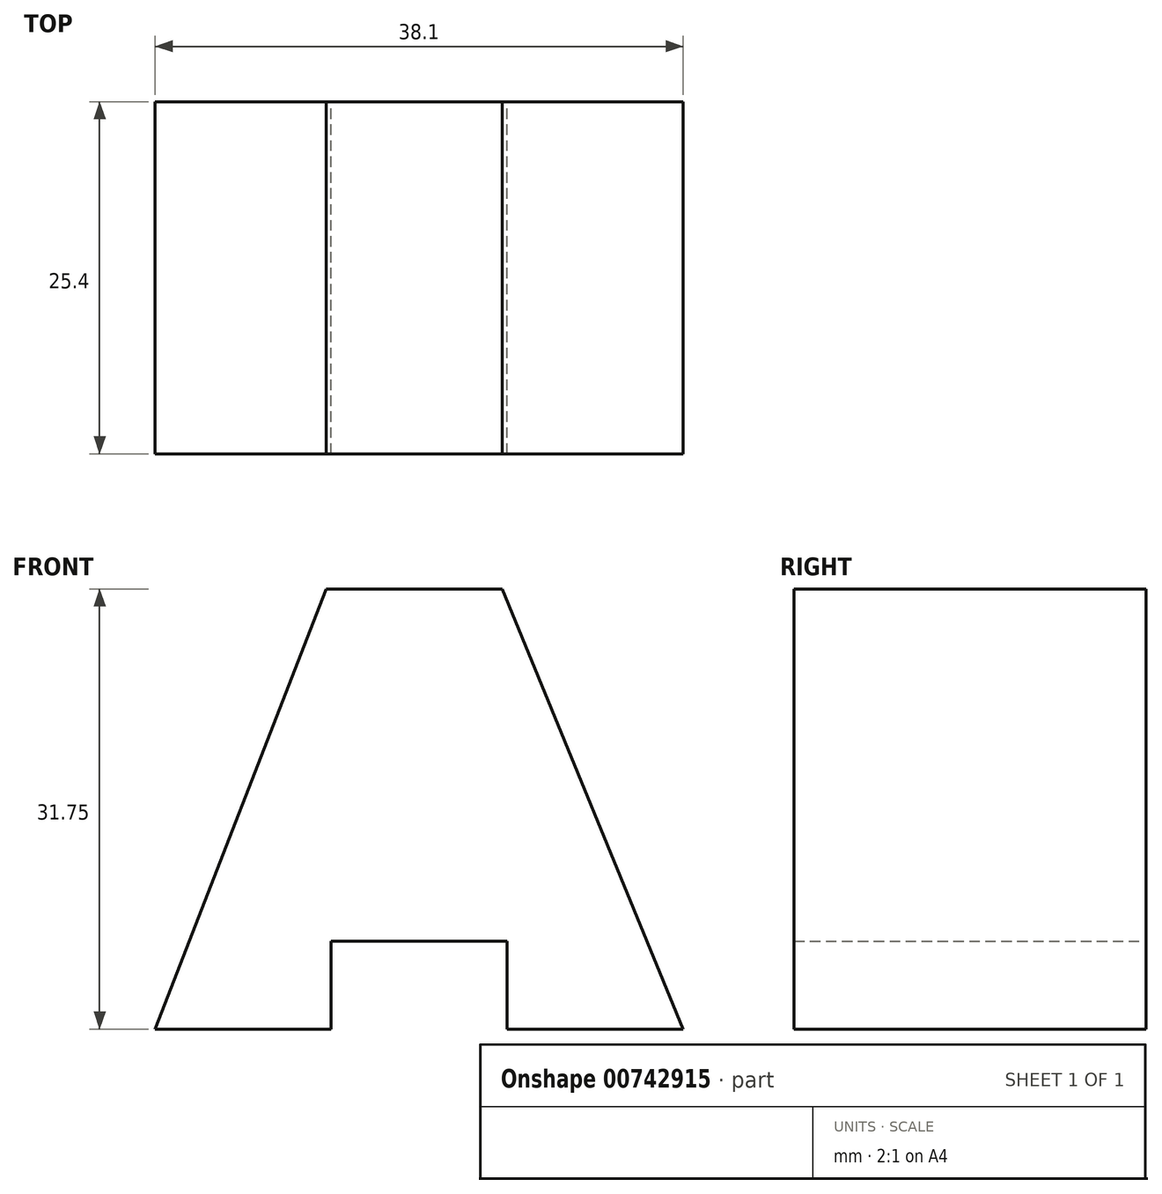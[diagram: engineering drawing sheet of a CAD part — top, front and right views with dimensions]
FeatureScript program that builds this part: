
annotation { "Feature Type Name" : "Feature", "Feature Type Description" : "" }
export const myFeature = defineFeature(function(context is Context, id is Id, definition is map)
    precondition{}
    {
        {
            var Q0;
            Q0=qCreatedBy(makeId("Front.planeOp"),FACE);
            var sketch = newSketch(context, id + "F0", { "sketchPlane" : qUnion([Q0])});
            skLineSegment(sketch, "E0", {"start": v(0, 0) * mm, "end": v(12.7, 0) * mm});
            skLineSegment(sketch, "E1", {"start": v(12.7, 0) * mm, "end": v(12.7, 6.35) * mm});
            skLineSegment(sketch, "E2", {"start": v(12.7, 6.35) * mm, "end": v(25.4, 6.35) * mm});
            skLineSegment(sketch, "E3", {"start": v(25.4, 6.35) * mm, "end": v(25.4, 0) * mm});
            skLineSegment(sketch, "E4", {"start": v(25.4, 0) * mm, "end": v(38.1, 0) * mm});
            skLineSegment(sketch, "E5", {"start": v(38.1, 0) * mm, "end": v(25.03, 31.75) * mm});
            skLineSegment(sketch, "E6", {"start": v(25.03, 31.75) * mm, "end": v(12.33, 31.75) * mm});
            skLineSegment(sketch, "E7", {"start": v(12.33, 31.75) * mm, "end": v(0, 0) * mm});
            skSolve(sketch);
        }
        {
            var Q0;
            Q0=makeQuery(id+"F0.imprint","IMPRINT",FACE,{"disambiguationData":[TD([[makeQuery(id+"F0.imprint","IMPRINT",EDGE,{"derivedFrom":sQuery(id+"F0.wireOp",EDGE,"E0")}),1.0]])]});
            extrude(context, id + "F1", {"entities" : qUnion([Q0]), "depth" : 25.4 * mm, "offsetDistance" : 25.4 * mm});
        }
    });
